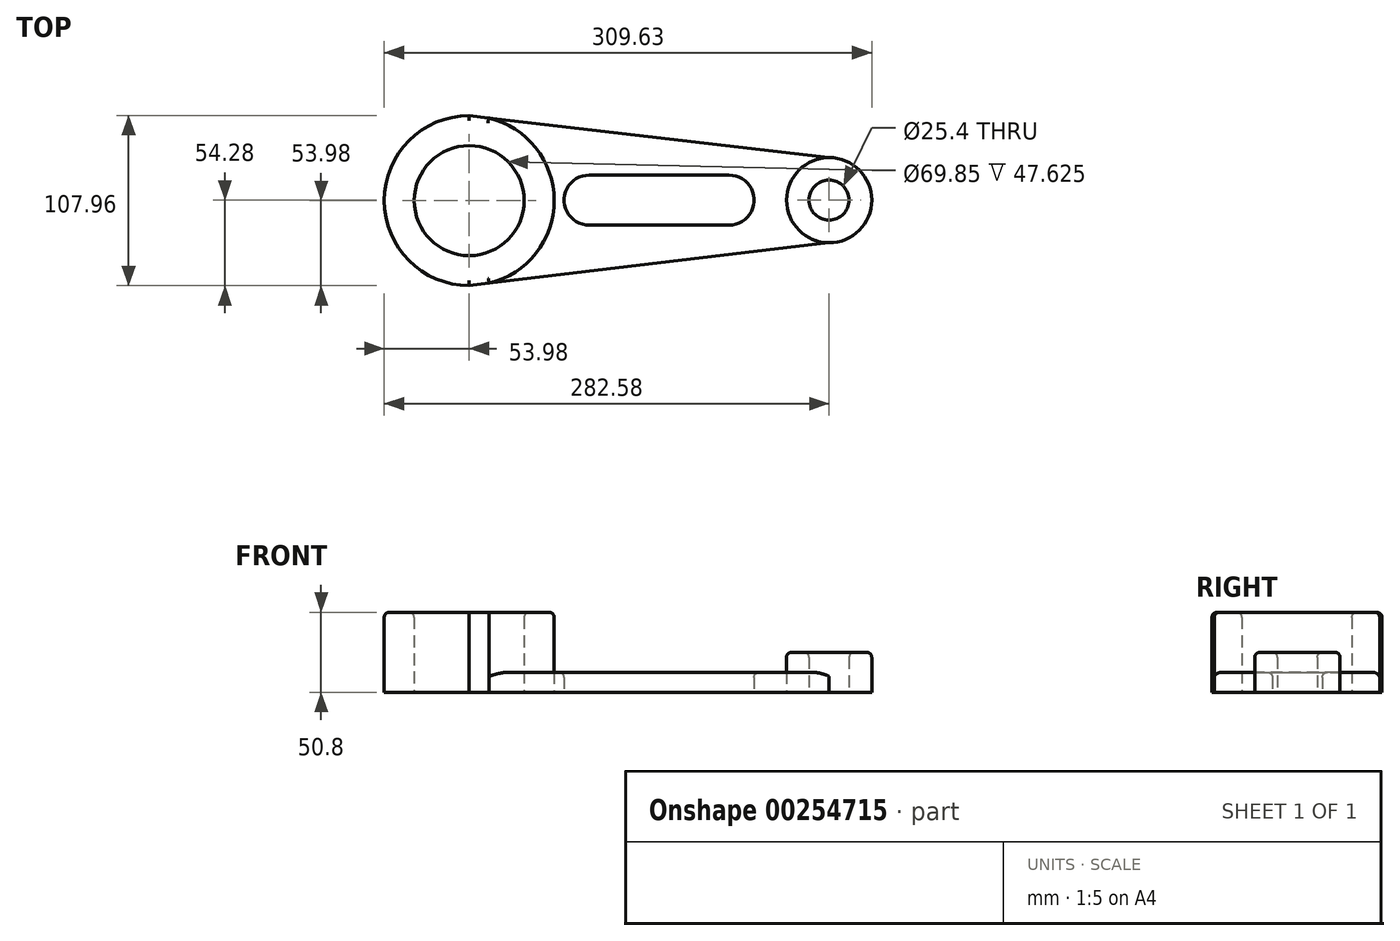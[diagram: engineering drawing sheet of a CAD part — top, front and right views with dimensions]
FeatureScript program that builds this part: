
annotation { "Feature Type Name" : "Feature", "Feature Type Description" : "" }
export const myFeature = defineFeature(function(context is Context, id is Id, definition is map)
    precondition{}
    {
        {
            var Q0;
            Q0=qCreatedBy(makeId("Top.planeOp"),FACE);
            var sketch = newSketch(context, id + "F0", { "sketchPlane" : qUnion([Q0])});
            skCircle(sketch, "E0", {"center": v(0, 0) * mm, "radius": 34.93 * mm});
            skCircle(sketch, "E1", {"center": v(0, 0) * mm, "radius": 53.98 * mm});
            skArc(sketch, "E2", {"start": v(76.2, 16.18) * mm, "mid": v(60.32, 0.3) * mm, "end": v(76.2, -15.57) * mm});
            skArc(sketch, "E3", {"start": v(165.1, -15.57) * mm, "mid": v(180.97, 0.3) * mm, "end": v(165.1, 16.18) * mm});
            skLineSegment(sketch, "E4", {"start": v(76.2, 16.18) * mm, "end": v(165.1, 16.18) * mm});
            skLineSegment(sketch, "E5", {"start": v(76.2, -15.57) * mm, "end": v(165.1, -15.57) * mm});
            skCircle(sketch, "E6", {"center": v(228.6, 0.3) * mm, "radius": 12.7 * mm});
            skCircle(sketch, "E7", {"center": v(228.6, 0.3) * mm, "radius": 27.05 * mm});
            skPoint(sketch, "E8", {"position": v(228.6, 27.35) * mm});
            skPoint(sketch, "E9", {"position": v(228.6, -26.75) * mm});
            skPoint(sketch, "E10", {"position": v(0, 53.98) * mm});
            skPoint(sketch, "E11", {"position": v(0, -53.98) * mm});
            skLineSegment(sketch, "E12", {"start": v(0, 53.98) * mm, "end": v(228.6, 27.35) * mm});
            skLineSegment(sketch, "E13", {"start": v(0, -53.98) * mm, "end": v(228.6, -26.75) * mm});
            skSolve(sketch);
        }
        {
            var Q0;
            {var subQ0=sQuery(id+"F0.wireOp",EDGE,"E12");var subQ1=sQuery(id+"F0.wireOp",EDGE,"E1");var subQ2=makeQuery(id+"F0.imprint","INTERSECT",VERTEX,{"disambiguationData":[OD(0.0)],"derivedFrom":[subQ1,subQ0]});Q0=makeQuery(id+"F0.imprint","IMPRINT",FACE,{"disambiguationData":[TD([[makeQuery(id+"F0.imprint","IMPRINT",EDGE,{"disambiguationData":[TD([[subQ2,1.0]])],"derivedFrom":subQ1}),1.0]])]});}
            var Q1;
            {var subQ0=sQuery(id+"F0.wireOp",EDGE,"E13");var subQ1=sQuery(id+"F0.wireOp",EDGE,"E1");var subQ2=makeQuery(id+"F0.imprint","INTERSECT",VERTEX,{"disambiguationData":[OD(0.0)],"derivedFrom":[subQ1,subQ0]});Q1=makeQuery(id+"F0.imprint","IMPRINT",FACE,{"disambiguationData":[TD([[makeQuery(id+"F0.imprint","IMPRINT",EDGE,{"disambiguationData":[TD([[subQ2,-1.0]])],"derivedFrom":subQ1}),1.0]])]});}
            var Q2;
            Q2=makeQuery(id+"F0.imprint","IMPRINT",FACE,{"disambiguationData":[TD([[makeQuery(id+"F0.imprint","IMPRINT",EDGE,{"derivedFrom":sQuery(id+"F0.wireOp",EDGE,"E0")}),-1.0]])]});
            extrude(context, id + "F1", {"entities" : qUnion([Q0, Q1, Q2]), "depth" : 50.8 * mm});
        }
        {
            var Q0;
            Q0=makeQuery(id+"F0.imprint","IMPRINT",FACE,{"disambiguationData":[TD([[makeQuery(id+"F0.imprint","IMPRINT",EDGE,{"derivedFrom":sQuery(id+"F0.wireOp",EDGE,"E6")}),-1.0]])]});
            extrude(context, id + "F2", {"entities" : qUnion([Q0]), "depth" : 25.4 * mm});
        }
        {
            var Q0;
            Q0=makeQuery(id+"F0.imprint","IMPRINT",FACE,{"disambiguationData":[TD([[makeQuery(id+"F0.imprint","IMPRINT",EDGE,{"derivedFrom":sQuery(id+"F0.wireOp",EDGE,"E2")}),-1.0]])]});
            extrude(context, id + "F3", {"entities" : qUnion([Q0]), "depth" : 12.7 * mm});
        }
        {
            var Q0;
            Q0=makeQuery(id+"F3.opExtrude","CAP_EDGE",EDGE,{"disambiguationData":[OSD([sQuery(id+"F0.wireOp",EDGE,"E13")])],"isStart":false});
            var Q1;
            Q1=makeQuery(id+"F3.opExtrude","CAP_EDGE",EDGE,{"disambiguationData":[OSD([sQuery(id+"F0.wireOp",EDGE,"E5")])],"isStart":false});
            var Q2;
            Q2=makeQuery(id+"F3.opExtrude","CAP_EDGE",EDGE,{"disambiguationData":[OSD([sQuery(id+"F0.wireOp",EDGE,"E12")])],"isStart":false});
            fillet(context, id + "F4", {"entities" : qUnion([Q0, Q1, Q2]), "radius" : 3.17 * mm, "tangentPropagation" : true, "allowEdgeOverflow" : false});
        }
        {
            var Q0;
            Q0=makeQuery(id+"F1.opExtrude","CAP_FACE",FACE,{"disambiguationData":[OSD([sQuery(id+"F0.wireOp",EDGE,"E0"),sQuery(id+"F0.wireOp",EDGE,"E1")])],"isStart":false});
            var Q1;
            Q1=makeQuery(id+"F1.opExtrude","CAP_EDGE",EDGE,{"disambiguationData":[OSD([sQuery(id+"F0.wireOp",EDGE,"E0")])],"isStart":false});
            fillet(context, id + "F5", {"entities" : qUnion([Q0, Q1]), "radius" : 3.17 * mm, "tangentPropagation" : true, "allowEdgeOverflow" : false});
        }
        {
            var Q0;
            Q0=makeQuery(id+"F2.opExtrude","CAP_EDGE",EDGE,{"disambiguationData":[OSD([sQuery(id+"F0.wireOp",EDGE,"E7")])],"isStart":false});
            var Q1;
            Q1=makeQuery(id+"F2.opExtrude","CAP_EDGE",EDGE,{"disambiguationData":[OSD([sQuery(id+"F0.wireOp",EDGE,"E6")])],"isStart":false});
            fillet(context, id + "F6", {"entities" : qUnion([Q0, Q1]), "radius" : 3.17 * mm, "tangentPropagation" : true, "allowEdgeOverflow" : false});
        }
    });
